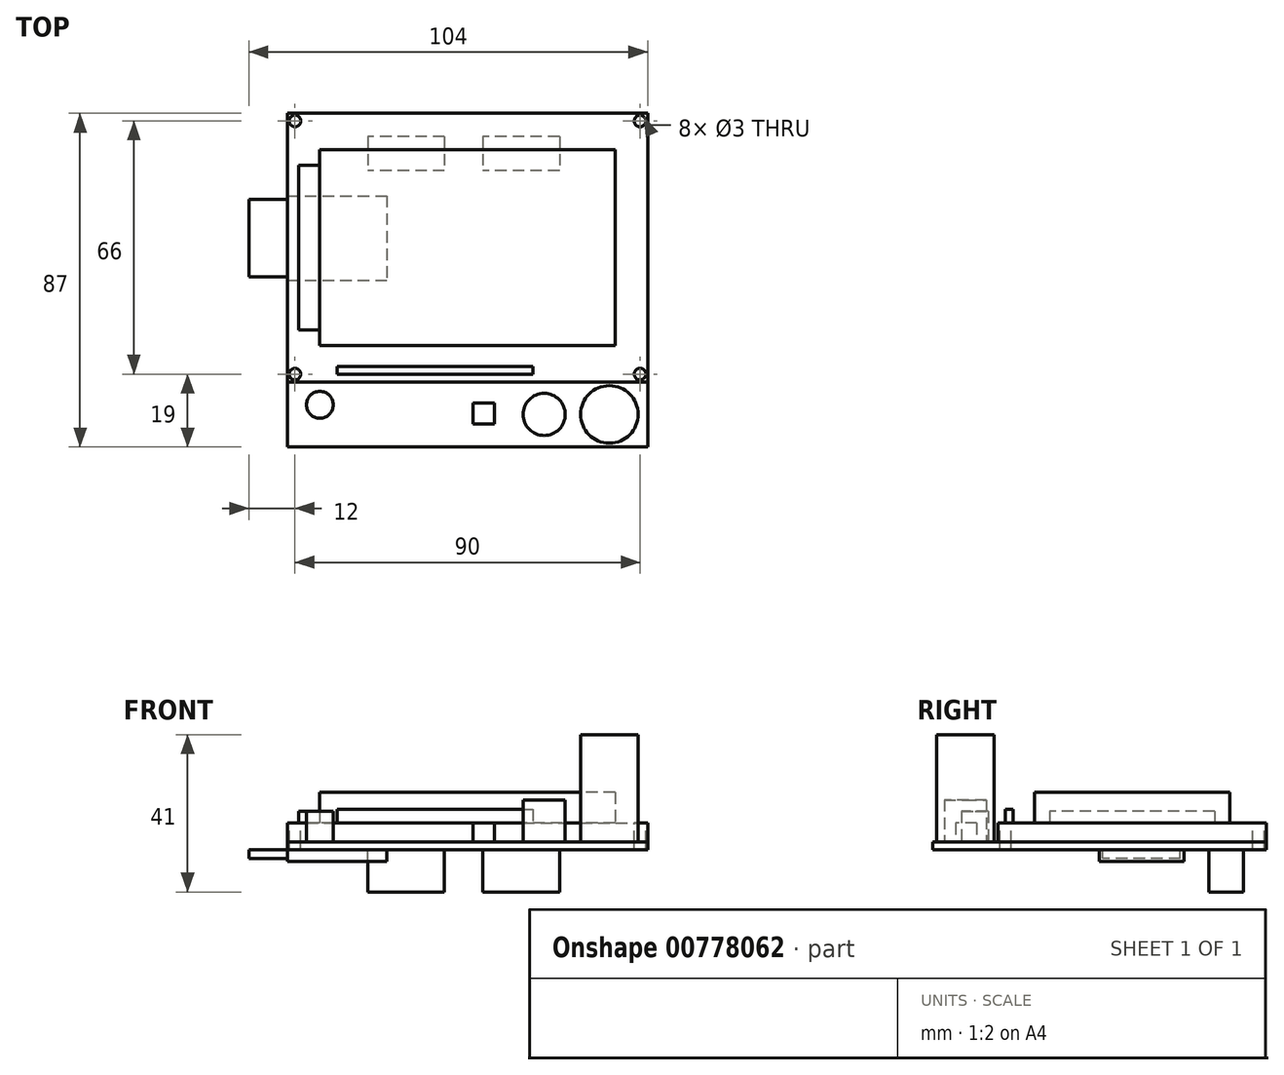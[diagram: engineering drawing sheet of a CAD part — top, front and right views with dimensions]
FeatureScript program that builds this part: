
annotation { "Feature Type Name" : "Feature", "Feature Type Description" : "" }
export const myFeature = defineFeature(function(context is Context, id is Id, definition is map)
    precondition{}
    {
        {
            var Q0;
            Q0=qCreatedBy(makeId("Top.planeOp"),FACE);
            var sketch = newSketch(context, id + "F0", { "sketchPlane" : qUnion([Q0])});
            skLineSegment(sketch, "E0.rect.bottom", {"start": v(47, 43.5) * mm, "end": v(-47, 43.5) * mm});
            skLineSegment(sketch, "E0.rect.top", {"start": v(47, -43.5) * mm, "end": v(-47, -43.5) * mm});
            skLineSegment(sketch, "E0.rect.left", {"start": v(47, 43.5) * mm, "end": v(47, -43.5) * mm});
            skLineSegment(sketch, "E0.rect.right", {"start": v(-47, 43.5) * mm, "end": v(-47, -43.5) * mm});
            skPoint(sketch, "E0.rect.middle", {"position": v(0, 0) * mm});
            skSolve(sketch);
        }
        {
            var Q0;
            Q0=makeQuery(id+"F0.imprint","IMPRINT",FACE,{"disambiguationData":[TD([[makeQuery(id+"F0.imprint","IMPRINT",EDGE,{"derivedFrom":sQuery(id+"F0.wireOp",EDGE,"E0.rect.bottom")}),1.0]])]});
            extrude(context, id + "F1", {"entities" : qUnion([Q0]), "depth" : 2 * mm});
        }
        {
            var Q0;
            Q0=makeQuery(id+"F1.opExtrude","CAP_FACE",FACE,{"disambiguationData":[OSD([sQuery(id+"F0.wireOp",EDGE,"E0.rect.bottom"),sQuery(id+"F0.wireOp",EDGE,"E0.rect.top"),sQuery(id+"F0.wireOp",EDGE,"E0.rect.left"),sQuery(id+"F0.wireOp",EDGE,"E0.rect.right")])],"isStart":false});
            var sketch = newSketch(context, id + "F2", { "sketchPlane" : qUnion([Q0])});
            skLineSegment(sketch, "E1.bottom", {"start": v(-47, 43.5) * mm, "end": v(47, 43.5) * mm});
            skLineSegment(sketch, "E1.top", {"start": v(-47, -26.5) * mm, "end": v(47, -26.5) * mm});
            skLineSegment(sketch, "E1.left", {"start": v(-47, 43.5) * mm, "end": v(-47, -26.5) * mm});
            skLineSegment(sketch, "E1.right", {"start": v(47, 43.5) * mm, "end": v(47, -26.5) * mm});
            skSolve(sketch);
        }
        {
            var Q0;
            Q0=makeQuery(id+"F2.imprint","IMPRINT",FACE,{"disambiguationData":[TD([[makeQuery(id+"F2.imprint","IMPRINT",EDGE,{"derivedFrom":sQuery(id+"F2.wireOp",EDGE,"E1.bottom")}),1.0]])]});
            extrude(context, id + "F3", {"entities" : qUnion([Q0]), "depth" : 5 * mm});
        }
        {
            var Q0;
            Q0=makeQuery(id+"F3.opExtrude","CAP_FACE",FACE,{"disambiguationData":[OSD([sQuery(id+"F2.wireOp",EDGE,"E1.bottom"),sQuery(id+"F2.wireOp",EDGE,"E1.top"),sQuery(id+"F2.wireOp",EDGE,"E1.left"),sQuery(id+"F2.wireOp",EDGE,"E1.right")])],"isStart":false});
            var sketch = newSketch(context, id + "F4", { "sketchPlane" : qUnion([Q0])});
            skLineSegment(sketch, "E2.rect.bottom", {"start": v(38.5, 34) * mm, "end": v(-38.5, 34) * mm});
            skLineSegment(sketch, "E2.rect.top", {"start": v(38.5, -17) * mm, "end": v(-38.5, -17) * mm});
            skLineSegment(sketch, "E2.rect.left", {"start": v(38.5, 34) * mm, "end": v(38.5, -17) * mm});
            skLineSegment(sketch, "E2.rect.right", {"start": v(-38.5, 34) * mm, "end": v(-38.5, -17) * mm});
            skPoint(sketch, "E2.rect.middle", {"position": v(0, 8.5) * mm});
            skSolve(sketch);
        }
        {
            var Q0;
            Q0=makeQuery(id+"F4.imprint","IMPRINT",FACE,{"disambiguationData":[TD([[makeQuery(id+"F4.imprint","IMPRINT",EDGE,{"derivedFrom":sQuery(id+"F4.wireOp",EDGE,"E2.rect.bottom")}),1.0]])]});
            extrude(context, id + "F5", {"entities" : qUnion([Q0]), "depth" : 8 * mm});
        }
        {
            var Q0;
            Q0=makeQuery(id+"F3.opExtrude","CAP_FACE",FACE,{"disambiguationData":[OSD([sQuery(id+"F2.wireOp",EDGE,"E1.bottom"),sQuery(id+"F2.wireOp",EDGE,"E1.top"),sQuery(id+"F2.wireOp",EDGE,"E1.left"),sQuery(id+"F2.wireOp",EDGE,"E1.right")])],"isStart":false});
            var sketch = newSketch(context, id + "F6", { "sketchPlane" : qUnion([Q0])});
            skLineSegment(sketch, "E3.bottom", {"start": v(-38.5, 30) * mm, "end": v(-44, 30) * mm});
            skLineSegment(sketch, "E3.top", {"start": v(-38.5, -13) * mm, "end": v(-44, -13) * mm});
            skLineSegment(sketch, "E3.left", {"start": v(-38.5, 30) * mm, "end": v(-38.5, -13) * mm});
            skLineSegment(sketch, "E3.right", {"start": v(-44, 30) * mm, "end": v(-44, -13) * mm});
            skSolve(sketch);
        }
        {
            var Q0;
            Q0=makeQuery(id+"F6.imprint","IMPRINT",FACE,{"disambiguationData":[TD([[makeQuery(id+"F6.imprint","IMPRINT",EDGE,{"derivedFrom":sQuery(id+"F6.wireOp",EDGE,"E3.bottom")}),1.0]])]});
            extrude(context, id + "F7", {"entities" : qUnion([Q0]), "depth" : 3 * mm});
        }
        {
            var Q0;
            Q0=makeQuery(id+"F1.opExtrude","CAP_FACE",FACE,{"disambiguationData":[OSD([sQuery(id+"F0.wireOp",EDGE,"E0.rect.bottom"),sQuery(id+"F0.wireOp",EDGE,"E0.rect.top"),sQuery(id+"F0.wireOp",EDGE,"E0.rect.left"),sQuery(id+"F0.wireOp",EDGE,"E0.rect.right")])],"isStart":false});
            var sketch = newSketch(context, id + "F8", { "sketchPlane" : qUnion([Q0])});
            skCircle(sketch, "E4", {"center": v(37, -35) * mm, "radius": 7.5 * mm});
            skSolve(sketch);
        }
        {
            var Q0;
            Q0=makeQuery(id+"F8.imprint","IMPRINT",FACE,{"disambiguationData":[TD([[makeQuery(id+"F8.imprint","IMPRINT",EDGE,{"derivedFrom":sQuery(id+"F8.wireOp",EDGE,"E4")}),1.0]])]});
            extrude(context, id + "F9", {"entities" : qUnion([Q0]), "depth" : 28 * mm});
        }
        {
            var Q0;
            Q0=makeQuery(id+"F1.opExtrude","CAP_FACE",FACE,{"disambiguationData":[OSD([sQuery(id+"F0.wireOp",EDGE,"E0.rect.bottom"),sQuery(id+"F0.wireOp",EDGE,"E0.rect.top"),sQuery(id+"F0.wireOp",EDGE,"E0.rect.left"),sQuery(id+"F0.wireOp",EDGE,"E0.rect.right")])],"isStart":false});
            var sketch = newSketch(context, id + "F10", { "sketchPlane" : qUnion([Q0])});
            skCircle(sketch, "E5", {"center": v(20, -35) * mm, "radius": 5.5 * mm});
            skSolve(sketch);
        }
        {
            var Q0;
            Q0=makeQuery(id+"F10.imprint","IMPRINT",FACE,{"disambiguationData":[TD([[makeQuery(id+"F10.imprint","IMPRINT",EDGE,{"derivedFrom":sQuery(id+"F10.wireOp",EDGE,"E5")}),1.0]])]});
            extrude(context, id + "F11", {"entities" : qUnion([Q0]), "depth" : 11 * mm});
        }
        {
            var Q0;
            Q0=makeQuery(id+"F1.opExtrude","CAP_FACE",FACE,{"disambiguationData":[OSD([sQuery(id+"F0.wireOp",EDGE,"E0.rect.bottom"),sQuery(id+"F0.wireOp",EDGE,"E0.rect.top"),sQuery(id+"F0.wireOp",EDGE,"E0.rect.left"),sQuery(id+"F0.wireOp",EDGE,"E0.rect.right")])],"isStart":false});
            var sketch = newSketch(context, id + "F12", { "sketchPlane" : qUnion([Q0])});
            skLineSegment(sketch, "E6.bottom", {"start": v(7, -32) * mm, "end": v(1.5, -32) * mm});
            skLineSegment(sketch, "E6.top", {"start": v(7, -37.5) * mm, "end": v(1.5, -37.5) * mm});
            skLineSegment(sketch, "E6.left", {"start": v(7, -32) * mm, "end": v(7, -37.5) * mm});
            skLineSegment(sketch, "E6.right", {"start": v(1.5, -32) * mm, "end": v(1.5, -37.5) * mm});
            skSolve(sketch);
        }
        {
            var Q0;
            Q0=makeQuery(id+"F12.imprint","IMPRINT",FACE,{"disambiguationData":[TD([[makeQuery(id+"F12.imprint","IMPRINT",EDGE,{"derivedFrom":sQuery(id+"F12.wireOp",EDGE,"E6.bottom")}),1.0]])]});
            extrude(context, id + "F13", {"entities" : qUnion([Q0]), "depth" : 5 * mm});
        }
        {
            var Q0;
            Q0=makeQuery(id+"F1.opExtrude","CAP_FACE",FACE,{"disambiguationData":[OSD([sQuery(id+"F0.wireOp",EDGE,"E0.rect.bottom"),sQuery(id+"F0.wireOp",EDGE,"E0.rect.top"),sQuery(id+"F0.wireOp",EDGE,"E0.rect.left"),sQuery(id+"F0.wireOp",EDGE,"E0.rect.right")])],"isStart":false});
            var sketch = newSketch(context, id + "F14", { "sketchPlane" : qUnion([Q0])});
            skCircle(sketch, "E7", {"center": v(-38.5, -32.5) * mm, "radius": 3.5 * mm});
            skSolve(sketch);
        }
        {
            var Q0;
            Q0=makeQuery(id+"F14.imprint","IMPRINT",FACE,{"disambiguationData":[TD([[makeQuery(id+"F14.imprint","IMPRINT",EDGE,{"derivedFrom":sQuery(id+"F14.wireOp",EDGE,"E7")}),1.0]])]});
            extrude(context, id + "F15", {"entities" : qUnion([Q0]), "depth" : 8 * mm});
        }
        {
            var Q0;
            Q0=makeQuery(id+"F3.opExtrude","CAP_FACE",FACE,{"disambiguationData":[OSD([sQuery(id+"F2.wireOp",EDGE,"E1.bottom"),sQuery(id+"F2.wireOp",EDGE,"E1.top"),sQuery(id+"F2.wireOp",EDGE,"E1.left"),sQuery(id+"F2.wireOp",EDGE,"E1.right")])],"isStart":false});
            var sketch = newSketch(context, id + "F16", { "sketchPlane" : qUnion([Q0])});
            skPoint(sketch, "E8", {"position": v(-45, 41.5) * mm});
            skPoint(sketch, "E9.MirrorP", {"position": v(45, 41.5) * mm});
            skPoint(sketch, "E10", {"position": v(45, -24.5) * mm});
            skPoint(sketch, "E11", {"position": v(-45, -24.5) * mm});
            skSolve(sketch);
        }
        {
            var Q0;
            Q0=sQuery(id+"F16.wireOp",VERTEX,"E8");
            var Q1;
            Q1=makeQuery(id+"F3.opExtrude","SWEPT_BODY",BODY,{"disambiguationData":[OSD([sQuery(id+"F2.wireOp",EDGE,"E1.bottom"),sQuery(id+"F2.wireOp",EDGE,"E1.top"),sQuery(id+"F2.wireOp",EDGE,"E1.left"),sQuery(id+"F2.wireOp",EDGE,"E1.right")])]});
            var Q2;
            Q2=makeQuery(id+"F1.opExtrude","SWEPT_BODY",BODY,{"disambiguationData":[OSD([sQuery(id+"F0.wireOp",EDGE,"E0.rect.bottom"),sQuery(id+"F0.wireOp",EDGE,"E0.rect.top"),sQuery(id+"F0.wireOp",EDGE,"E0.rect.left"),sQuery(id+"F0.wireOp",EDGE,"E0.rect.right")])]});
            hole(context, id + "F17", {"style" : HoleStyle.SIMPLE, "holeDiameter" : 3 * mm, "endStyle" : HoleEndStyle.BLIND, "holeDepth" : 20 * mm, "locations" : qUnion([Q0]), "scope" : qUnion([Q1, Q2])});
        }
        {
            var Q0;
            Q0=sQuery(id+"F16.wireOp",VERTEX,"E9.MirrorP");
            var Q1;
            Q1=sQuery(id+"F16.wireOp",VERTEX,"E10");
            var Q2;
            Q2=sQuery(id+"F16.wireOp",VERTEX,"E11");
            var Q3;
            Q3=makeQuery(id+"F3.opExtrude","SWEPT_BODY",BODY,{"disambiguationData":[OSD([sQuery(id+"F2.wireOp",EDGE,"E1.bottom"),sQuery(id+"F2.wireOp",EDGE,"E1.top"),sQuery(id+"F2.wireOp",EDGE,"E1.left"),sQuery(id+"F2.wireOp",EDGE,"E1.right")])]});
            var Q4;
            Q4=makeQuery(id+"F1.opExtrude","SWEPT_BODY",BODY,{"disambiguationData":[OSD([sQuery(id+"F0.wireOp",EDGE,"E0.rect.bottom"),sQuery(id+"F0.wireOp",EDGE,"E0.rect.top"),sQuery(id+"F0.wireOp",EDGE,"E0.rect.left"),sQuery(id+"F0.wireOp",EDGE,"E0.rect.right")])]});
            hole(context, id + "F18", {"style" : HoleStyle.SIMPLE, "holeDiameter" : 3 * mm, "endStyle" : HoleEndStyle.THROUGH, "locations" : qUnion([Q0, Q1, Q2]), "scope" : qUnion([Q3, Q4])});
        }
        {
            var Q0;
            Q0=makeQuery(id+"F16.imprint","IMPRINT",FACE,{"disambiguationData":[TD([[makeQuery(id+"F16.imprint","IMPRINT",EDGE,{"derivedFrom":makeQuery(id+"F3.opExtrude","CAP_EDGE",EDGE,{"disambiguationData":[OSD([sQuery(id+"F2.wireOp",EDGE,"E1.bottom")])],"isStart":false})}),1.0]])]});
            var sketch = newSketch(context, id + "F19", { "sketchPlane" : qUnion([Q0])});
            skLineSegment(sketch, "E12.bottom", {"start": v(-34, -24.5) * mm, "end": v(17, -24.5) * mm});
            skLineSegment(sketch, "E12.top", {"start": v(-34, -22.5) * mm, "end": v(17, -22.5) * mm});
            skLineSegment(sketch, "E12.left", {"start": v(-34, -24.5) * mm, "end": v(-34, -22.5) * mm});
            skLineSegment(sketch, "E12.right", {"start": v(17, -24.5) * mm, "end": v(17, -22.5) * mm});
            skSolve(sketch);
        }
        {
            var Q0;
            Q0=makeQuery(id+"F19.imprint","IMPRINT",FACE,{"disambiguationData":[TD([[makeQuery(id+"F19.imprint","IMPRINT",EDGE,{"derivedFrom":sQuery(id+"F19.wireOp",EDGE,"E12.bottom")}),1.0]])]});
            extrude(context, id + "F20", {"entities" : qUnion([Q0]), "depth" : 3.5 * mm});
        }
        {
            var Q0;
            Q0=makeQuery(id+"F1.opExtrude","CAP_FACE",FACE,{"disambiguationData":[OSD([sQuery(id+"F0.wireOp",EDGE,"E0.rect.bottom"),sQuery(id+"F0.wireOp",EDGE,"E0.rect.top"),sQuery(id+"F0.wireOp",EDGE,"E0.rect.left"),sQuery(id+"F0.wireOp",EDGE,"E0.rect.right")])],"isStart":true});
            var sketch = newSketch(context, id + "F21", { "sketchPlane" : qUnion([Q0])});
            skLineSegment(sketch, "E13.bottom", {"start": v(-47, -22) * mm, "end": v(-21, -22) * mm});
            skLineSegment(sketch, "E13.top", {"start": v(-47, 0) * mm, "end": v(-21, 0) * mm});
            skLineSegment(sketch, "E13.left", {"start": v(-47, -22) * mm, "end": v(-47, 0) * mm});
            skLineSegment(sketch, "E13.right", {"start": v(-21, -22) * mm, "end": v(-21, 0) * mm});
            skSolve(sketch);
        }
        {
            var Q0;
            Q0=makeQuery(id+"F21.imprint","IMPRINT",FACE,{"disambiguationData":[TD([[makeQuery(id+"F21.imprint","IMPRINT",EDGE,{"derivedFrom":sQuery(id+"F21.wireOp",EDGE,"E13.bottom")}),1.0]])]});
            extrude(context, id + "F22", {"entities" : qUnion([Q0]), "operationType" : NewBodyOperationType.ADD, "depth" : 3 * mm});
        }
        {
            var Q0;
            Q0=makeQuery(id+"F1.opExtrude","CAP_FACE",FACE,{"disambiguationData":[OSD([sQuery(id+"F0.wireOp",EDGE,"E0.rect.bottom"),sQuery(id+"F0.wireOp",EDGE,"E0.rect.top"),sQuery(id+"F0.wireOp",EDGE,"E0.rect.left"),sQuery(id+"F0.wireOp",EDGE,"E0.rect.right")])],"isStart":true});
            var sketch = newSketch(context, id + "F23", { "sketchPlane" : qUnion([Q0])});
            skLineSegment(sketch, "E14.bottom", {"start": v(24, -37.5) * mm, "end": v(4, -37.5) * mm});
            skLineSegment(sketch, "E14.top", {"start": v(24, -28.5) * mm, "end": v(4, -28.5) * mm});
            skLineSegment(sketch, "E14.left", {"start": v(24, -37.5) * mm, "end": v(24, -28.5) * mm});
            skLineSegment(sketch, "E14.right", {"start": v(4, -37.5) * mm, "end": v(4, -28.5) * mm});
            skLineSegment(sketch, "E15.bottom", {"start": v(-6, -37.5) * mm, "end": v(-26, -37.5) * mm});
            skLineSegment(sketch, "E15.top", {"start": v(-6, -28.5) * mm, "end": v(-26, -28.5) * mm});
            skLineSegment(sketch, "E15.left", {"start": v(-6, -37.5) * mm, "end": v(-6, -28.5) * mm});
            skLineSegment(sketch, "E15.right", {"start": v(-26, -37.5) * mm, "end": v(-26, -28.5) * mm});
            skSolve(sketch);
        }
        {
            var Q0;
            Q0=qSketchRegion(id+"F23",true);
            extrude(context, id + "F24", {"entities" : qUnion([Q0]), "operationType" : NewBodyOperationType.ADD, "depth" : 11 * mm});
        }
        {
            var Q0;
            Q0=makeQuery(id+"F22.boolean.opBoolean","MERGE",FACE,{"derivedFrom":[makeQuery(id+"F1.opExtrude","SWEPT_FACE",FACE,{"disambiguationData":[OSD([sQuery(id+"F0.wireOp",EDGE,"E0.rect.right")])]}),makeQuery(id+"F22.opExtrude","SWEPT_FACE",FACE,{"disambiguationData":[OSD([sQuery(id+"F21.wireOp",EDGE,"E13.left")])]})]});
            var sketch = newSketch(context, id + "F25", { "sketchPlane" : qUnion([Q0])});
            skLineSegment(sketch, "E16.bottom", {"start": v(-21.06, -2.3) * mm, "end": v(-0.87, -2.3) * mm});
            skLineSegment(sketch, "E16.top", {"start": v(-21.06, 0) * mm, "end": v(-0.87, 0) * mm});
            skLineSegment(sketch, "E16.left", {"start": v(-21.06, -2.3) * mm, "end": v(-21.06, 0) * mm});
            skLineSegment(sketch, "E16.right", {"start": v(-0.87, -2.3) * mm, "end": v(-0.87, 0) * mm});
            skSolve(sketch);
        }
        {
            var Q0;
            Q0=qSketchRegion(id+"F25",true);
            var Q1;
            Q1=makeQuery(id+"F25.imprint","IMPRINT",FACE,{"disambiguationData":[TD([[makeQuery(id+"F25.imprint","IMPRINT",EDGE,{"derivedFrom":sQuery(id+"F25.wireOp",EDGE,"E16.bottom")}),1.0]])]});
            extrude(context, id + "F26", {"entities" : qUnion([Q0, Q1]), "operationType" : NewBodyOperationType.ADD, "depth" : 10 * mm});
        }
    });
